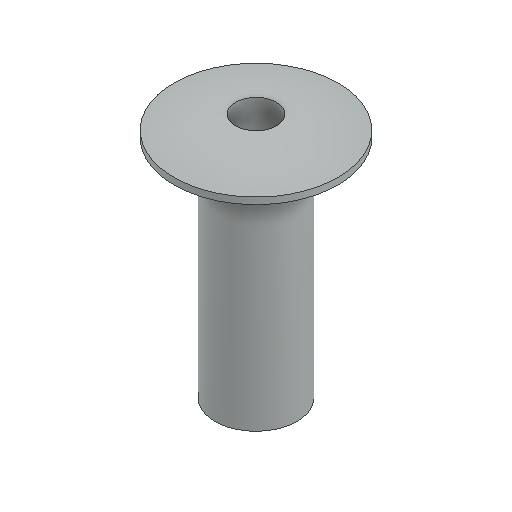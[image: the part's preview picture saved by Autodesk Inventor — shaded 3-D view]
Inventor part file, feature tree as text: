
AUTODESK INVENTOR PART (.ipt)
format: ipt  version: 2024.1 (Build 281209000, 209)  size: 113,664 bytes
history: native  units: in
note: dims shown in document units (in); Inventor stores cm internally (conversion verified against a paired STEP export)
features: revolve x1
ambient origin geometry x8: Origin, YZ Plane, XZ Plane, XY Plane, X Axis, Y Axis, Z Axis, Center Point
bodies: Solid1 (feature_tree)
feature tree (1):
  revolve  "Revolve1"  [1 undecoded]
note: 1 required parameter value undecoded (feature->parameter linkage not recoverable at this tier; creation-order binding heuristic only, values carry confidence <= 0.55)
